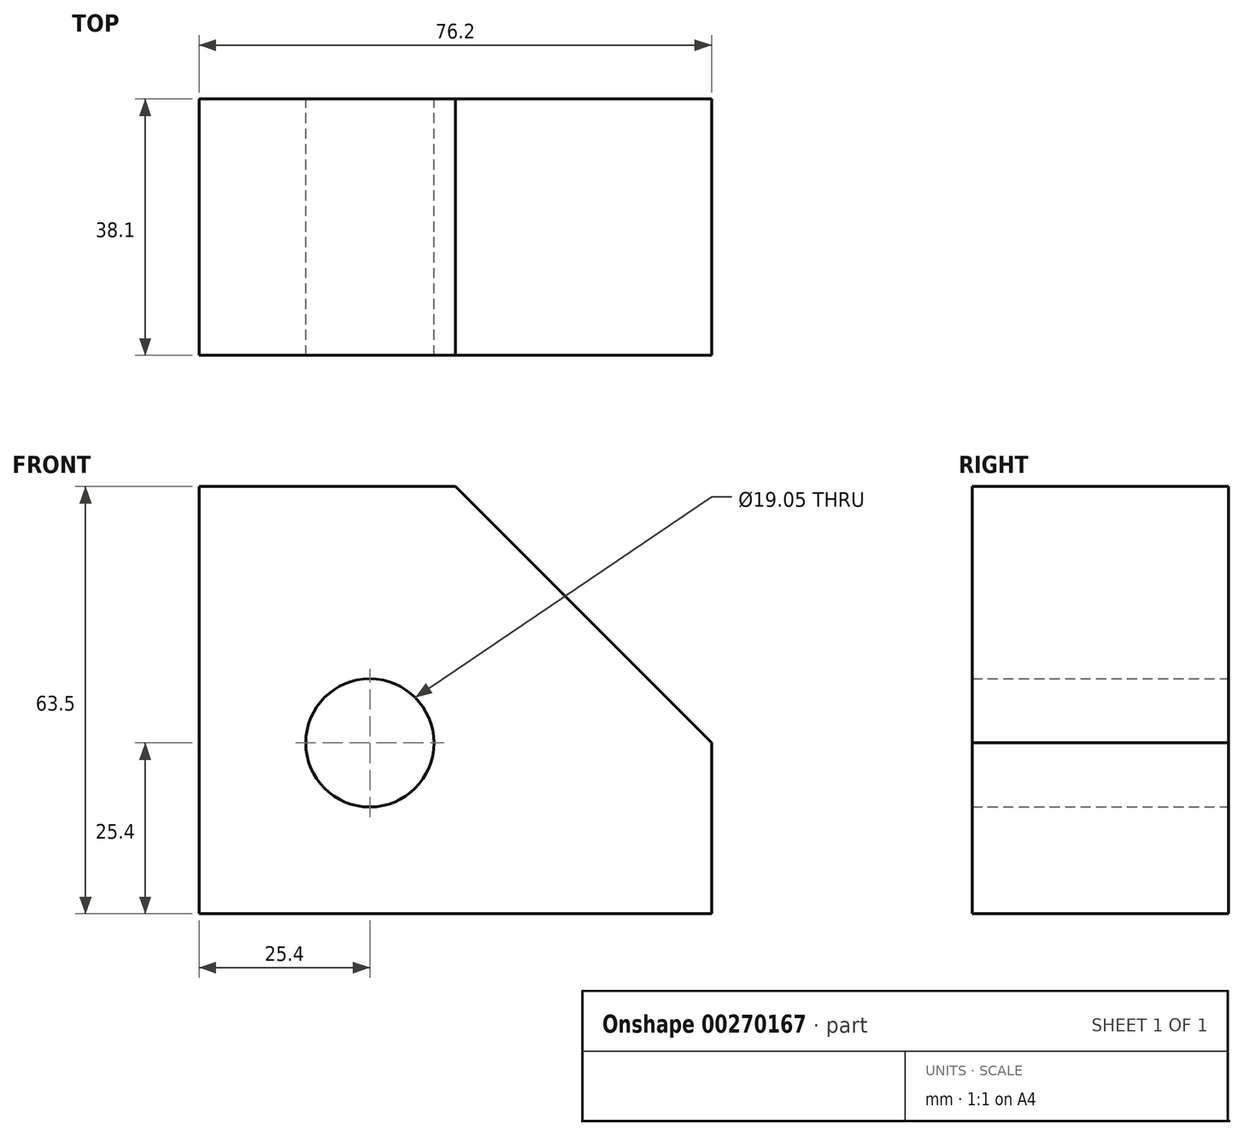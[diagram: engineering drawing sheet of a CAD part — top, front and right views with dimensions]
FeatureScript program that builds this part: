
annotation { "Feature Type Name" : "Feature", "Feature Type Description" : "" }
export const myFeature = defineFeature(function(context is Context, id is Id, definition is map)
    precondition{}
    {
        {
            var Q0;
            Q0=qCreatedBy(makeId("Front.planeOp"),FACE);
            var sketch = newSketch(context, id + "F0", { "sketchPlane" : qUnion([Q0])});
            skLineSegment(sketch, "E0.bottom", {"start": v(0, 0) * mm, "end": v(76.2, 0) * mm});
            skLineSegment(sketch, "E0.top", {"start": v(0, 63.5) * mm, "end": v(38.1, 63.5) * mm});
            skLineSegment(sketch, "E0.left", {"start": v(0, 0) * mm, "end": v(0, 63.5) * mm});
            skLineSegment(sketch, "E0.right", {"start": v(76.2, 0) * mm, "end": v(76.2, 25.4) * mm});
            skLineSegment(sketch, "E1", {"start": v(38.1, 63.5) * mm, "end": v(76.2, 25.4) * mm});
            skCircle(sketch, "E2", {"center": v(25.4, 25.4) * mm, "radius": 9.53 * mm});
            skSolve(sketch);
        }
        {
            var Q0;
            Q0=makeQuery(id+"F0.imprint","IMPRINT",FACE,{"disambiguationData":[TD([[makeQuery(id+"F0.imprint","IMPRINT",EDGE,{"derivedFrom":sQuery(id+"F0.wireOp",EDGE,"E0.bottom")}),1.0]])]});
            extrude(context, id + "F1", {"entities" : qUnion([Q0]), "depth" : 38.1 * mm});
        }
    });
